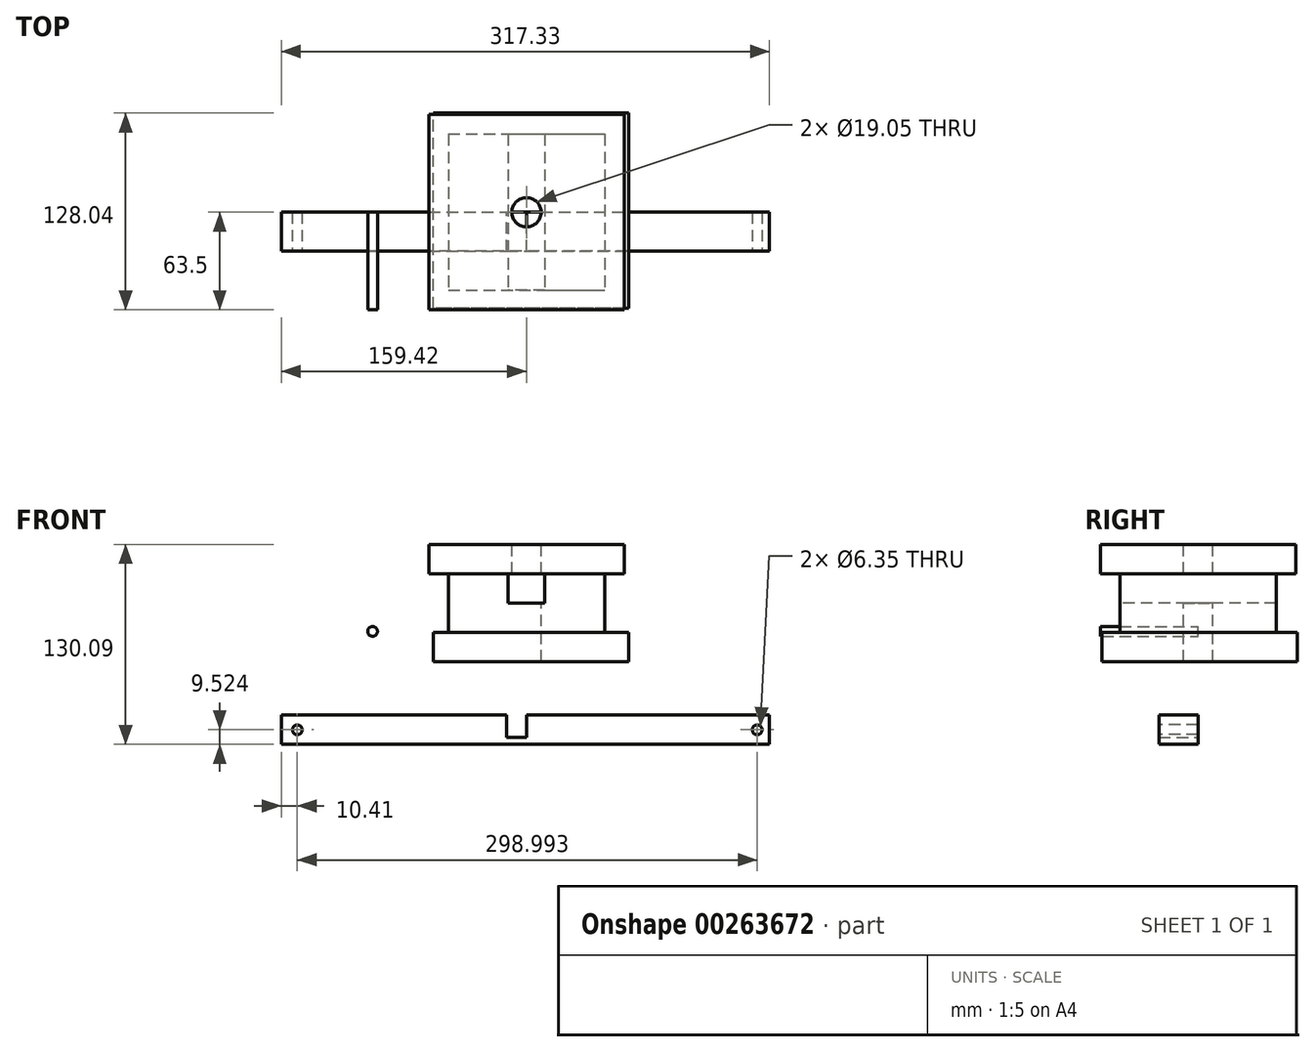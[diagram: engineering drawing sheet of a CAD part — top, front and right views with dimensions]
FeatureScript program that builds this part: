
annotation { "Feature Type Name" : "Feature", "Feature Type Description" : "" }
export const myFeature = defineFeature(function(context is Context, id is Id, definition is map)
    precondition{}
    {
        {
            var Q0;
            Q0=qCreatedBy(makeId("Top.planeOp"),FACE);
            var sketch = newSketch(context, id + "F0", { "sketchPlane" : qUnion([Q0])});
            skLineSegment(sketch, "E0", {"start": v(-60.56, 64.54) * mm, "end": v(66.44, 64.54) * mm});
            skLineSegment(sketch, "E1", {"start": v(66.44, 64.54) * mm, "end": v(66.44, -62.46) * mm});
            skLineSegment(sketch, "E2", {"start": v(66.44, -62.46) * mm, "end": v(-60.56, -62.46) * mm});
            skLineSegment(sketch, "E3", {"start": v(-60.56, -62.46) * mm, "end": v(-60.56, 64.54) * mm});
            skSolve(sketch);
        }
        {
            var Q0;
            Q0=makeQuery(id+"F0.imprint","IMPRINT",FACE,{"disambiguationData":[TD([[makeQuery(id+"F0.imprint","IMPRINT",EDGE,{"derivedFrom":sQuery(id+"F0.wireOp",EDGE,"E0")}),-1.0]])]});
            extrude(context, id + "F1", {"entities" : qUnion([Q0]), "depth" : 19.05 * mm});
        }
        {
            var Q0;
            Q0=makeQuery(id+"F1.opExtrude","CAP_FACE",FACE,{"disambiguationData":[OSD([sQuery(id+"F0.wireOp",EDGE,"E0"),sQuery(id+"F0.wireOp",EDGE,"E1"),sQuery(id+"F0.wireOp",EDGE,"E2"),sQuery(id+"F0.wireOp",EDGE,"E3")])],"isStart":false});
            var sketch = newSketch(context, id + "F2", { "sketchPlane" : qUnion([Q0])});
            skLineSegment(sketch, "E4.bottom", {"start": v(-50.8, 50.8) * mm, "end": v(50.8, 50.8) * mm});
            skLineSegment(sketch, "E4.top", {"start": v(-50.8, -50.8) * mm, "end": v(50.8, -50.8) * mm});
            skLineSegment(sketch, "E4.left", {"start": v(-50.8, 50.8) * mm, "end": v(-50.8, -50.8) * mm});
            skLineSegment(sketch, "E4.right", {"start": v(50.8, 50.8) * mm, "end": v(50.8, -50.8) * mm});
            skPoint(sketch, "E4.middle", {"position": v(0, 0) * mm});
            skSolve(sketch);
        }
        {
            var Q0;
            Q0=makeQuery(id+"F2.imprint","IMPRINT",FACE,{"disambiguationData":[TD([[makeQuery(id+"F2.imprint","IMPRINT",EDGE,{"derivedFrom":sQuery(id+"F2.wireOp",EDGE,"E4.bottom")}),-1.0]])]});
            extrude(context, id + "F3", {"entities" : qUnion([Q0]), "operationType" : NewBodyOperationType.ADD, "depth" : 38.1 * mm});
        }
        {
            var Q0;
            Q0=makeQuery(id+"F3.opExtrude","CAP_FACE",FACE,{"disambiguationData":[OSD([sQuery(id+"F2.wireOp",EDGE,"E4.bottom"),sQuery(id+"F2.wireOp",EDGE,"E4.top"),sQuery(id+"F2.wireOp",EDGE,"E4.left"),sQuery(id+"F2.wireOp",EDGE,"E4.right")])],"isStart":false});
            var sketch = newSketch(context, id + "F4", { "sketchPlane" : qUnion([Q0])});
            skLineSegment(sketch, "E5.bottom", {"start": v(-63.5, 63.5) * mm, "end": v(63.5, 63.5) * mm});
            skLineSegment(sketch, "E5.top", {"start": v(-63.5, -63.5) * mm, "end": v(63.5, -63.5) * mm});
            skLineSegment(sketch, "E5.left", {"start": v(-63.5, 63.5) * mm, "end": v(-63.5, -63.5) * mm});
            skLineSegment(sketch, "E5.right", {"start": v(63.5, 63.5) * mm, "end": v(63.5, -63.5) * mm});
            skPoint(sketch, "E5.middle", {"position": v(0, 0) * mm});
            skSolve(sketch);
        }
        {
            var Q0;
            Q0=makeQuery(id+"F4.imprint","IMPRINT",FACE,{"disambiguationData":[TD([[makeQuery(id+"F4.imprint","IMPRINT",EDGE,{"derivedFrom":sQuery(id+"F4.wireOp",EDGE,"E5.bottom")}),-1.0]])]});
            var Q1;
            Q1=makeQuery(id+"F4.imprint","IMPRINT",FACE,{"disambiguationData":[TD([[makeQuery(id+"F4.imprint","IMPRINT",EDGE,{"derivedFrom":makeQuery(id+"F3.opExtrude","CAP_EDGE",EDGE,{"disambiguationData":[OSD([sQuery(id+"F2.wireOp",EDGE,"E4.bottom")])],"isStart":false})}),-1.0]])]});
            extrude(context, id + "F5", {"entities" : qUnion([Q0, Q1]), "operationType" : NewBodyOperationType.ADD, "depth" : 19.05 * mm});
        }
        {
            var Q0;
            Q0=makeQuery(id+"F3.opExtrude","SWEPT_FACE",FACE,{"disambiguationData":[OSD([sQuery(id+"F2.wireOp",EDGE,"E4.top")])]});
            var sketch = newSketch(context, id + "F6", { "sketchPlane" : qUnion([Q0])});
            skPoint(sketch, "E6.start.orphan", {"position": v(-14.24, 44.1) * mm});
            skPoint(sketch, "E7.end.orphan", {"position": v(4.33, 44.1) * mm});
            skLineSegment(sketch, "E8", {"start": v(0, 19.05) * mm, "end": v(0, 38.1) * mm});
            skLineSegment(sketch, "E9.bottom", {"start": v(11.9, 57.15) * mm, "end": v(-11.9, 57.15) * mm});
            skLineSegment(sketch, "E9.top", {"start": v(11.9, 38.1) * mm, "end": v(-11.9, 38.1) * mm});
            skLineSegment(sketch, "E9.left", {"start": v(11.9, 57.15) * mm, "end": v(11.9, 38.1) * mm});
            skLineSegment(sketch, "E9.right", {"start": v(-11.9, 57.15) * mm, "end": v(-11.9, 38.1) * mm});
            skPoint(sketch, "E9.middle", {"position": v(0, 47.63) * mm});
            skPoint(sketch, "E10.start.orphan", {"position": v(0, 57.15) * mm});
            skSolve(sketch);
        }
        {
            var Q0;
            Q0=makeQuery(id+"F5.opExtrude","CAP_FACE",FACE,{"disambiguationData":[OSD([sQuery(id+"F4.wireOp",EDGE,"E5.bottom"),sQuery(id+"F4.wireOp",EDGE,"E5.top"),sQuery(id+"F4.wireOp",EDGE,"E5.left"),sQuery(id+"F4.wireOp",EDGE,"E5.right")])],"isStart":false});
            var sketch = newSketch(context, id + "F7", { "sketchPlane" : qUnion([Q0])});
            skPoint(sketch, "E11.start.orphan", {"position": v(-7.43, 0) * mm});
            skLineSegment(sketch, "E12", {"start": v(-7.43, 0) * mm, "end": v(0, 0) * mm});
            skSolve(sketch);
        }
        {
            var Q0;
            Q0=sQuery(id+"F7.wireOp",VERTEX,"E12.end");
            var Q1;
            Q1=makeQuery(id+"F1.opExtrude","SWEPT_BODY",BODY,{"disambiguationData":[OSD([sQuery(id+"F0.wireOp",EDGE,"E0"),sQuery(id+"F0.wireOp",EDGE,"E1"),sQuery(id+"F0.wireOp",EDGE,"E2"),sQuery(id+"F0.wireOp",EDGE,"E3")])]});
            hole(context, id + "F8", {"style" : HoleStyle.SIMPLE, "endStyle" : HoleEndStyle.THROUGH, "holeDiameter" : 19.05 * mm, "tappedDepth" : 12.7 * mm, "tapClearance" : 3, "locations" : qUnion([Q0]), "scope" : qUnion([Q1])});
        }
        {
            var Q0;
            Q0=makeQuery(id+"F6.imprint","IMPRINT",FACE,{"disambiguationData":[TD([[makeQuery(id+"F6.imprint","IMPRINT",EDGE,{"derivedFrom":sQuery(id+"F6.wireOp",EDGE,"E9.bottom")}),-1.0]])]});
            extrude(context, id + "F9", {"entities" : qUnion([Q0]), "operationType" : NewBodyOperationType.REMOVE, "endBound" : BoundingType.THROUGH_ALL, "oppositeDirection" : true, "depth" : 25.4 * mm});
        }
        {
            var Q0;
            Q0=qCreatedBy(makeId("Front.planeOp"),FACE);
            var sketch = newSketch(context, id + "F10", { "sketchPlane" : qUnion([Q0])});
            skLineSegment(sketch, "E13", {"start": v(157.91, -34.84) * mm, "end": v(157.91, -53.9) * mm});
            skLineSegment(sketch, "E14", {"start": v(157.91, -53.9) * mm, "end": v(-159.42, -53.9) * mm});
            skPoint(sketch, "E15.end.orphan", {"position": v(-164.43, -34.84) * mm});
            skLineSegment(sketch, "E16", {"start": v(-159.42, -34.84) * mm, "end": v(-159.42, -53.9) * mm});
            skLineSegment(sketch, "E17", {"start": v(-159.42, -34.84) * mm, "end": v(-13.03, -34.84) * mm});
            skPoint(sketch, "E18.end.orphan", {"position": v(18.55, -45.37) * mm});
            skPoint(sketch, "E19.end.orphan", {"position": v(0, -34.84) * mm});
            skLineSegment(sketch, "E20", {"start": v(18.55, -34.84) * mm, "end": v(157.91, -34.84) * mm});
            skLineSegment(sketch, "E21", {"start": v(0, -34.84) * mm, "end": v(18.55, -34.84) * mm});
            skPoint(sketch, "E22.end.orphan", {"position": v(14.04, -45.37) * mm});
            skPoint(sketch, "E23.end.orphan", {"position": v(0, -45.37) * mm});
            skPoint(sketch, "E24.end.orphan", {"position": v(-13.03, -45.37) * mm});
            skLineSegment(sketch, "E25", {"start": v(-13.03, -34.84) * mm, "end": v(-13.03, -49.38) * mm});
            skLineSegment(sketch, "E26", {"start": v(-13.03, -49.38) * mm, "end": v(0, -49.38) * mm});
            skLineSegment(sketch, "E27", {"start": v(0, -49.38) * mm, "end": v(0, -34.84) * mm});
            skLineSegment(sketch, "E28", {"start": v(-13.03, -44.37) * mm, "end": v(0, -44.37) * mm});
            skPoint(sketch, "E28.startSnap0", {"position": v(-159.42, -44.37) * mm});
            skPoint(sketch, "E29.orphan", {"position": v(-150.26, -44.37) * mm});
            skSolve(sketch);
        }
        {
            var Q0;
            Q0=makeQuery(id+"F10.imprint","IMPRINT",FACE,{"disambiguationData":[TD([[makeQuery(id+"F10.imprint","IMPRINT",EDGE,{"derivedFrom":sQuery(id+"F10.wireOp",EDGE,"E13")}),-1.0]])]});
            extrude(context, id + "F11", {"entities" : qUnion([Q0]), "depth" : 25.4 * mm});
        }
        {
            var Q0;
            Q0=makeQuery(id+"F11.opExtrude","CAP_FACE",FACE,{"disambiguationData":[OSD([sQuery(id+"F10.wireOp",EDGE,"E13"),sQuery(id+"F10.wireOp",EDGE,"E14"),sQuery(id+"F10.wireOp",EDGE,"E16"),sQuery(id+"F10.wireOp",EDGE,"E17"),sQuery(id+"F10.wireOp",EDGE,"E20"),sQuery(id+"F10.wireOp",EDGE,"E21"),sQuery(id+"F10.wireOp",EDGE,"E25"),sQuery(id+"F10.wireOp",EDGE,"E26"),sQuery(id+"F10.wireOp",EDGE,"E27")])],"isStart":false});
            var sketch = newSketch(context, id + "F12", { "sketchPlane" : qUnion([Q0])});
            skLineSegment(sketch, "E30", {"start": v(-149.01, -44.37) * mm, "end": v(149.98, -44.37) * mm});
            skPoint(sketch, "E30.startSnap0", {"position": v(-159.42, -44.37) * mm});
            skPoint(sketch, "E30.endSnap0", {"position": v(157.91, -44.37) * mm});
            skSolve(sketch);
        }
        {
            var Q0;
            Q0=sQuery(id+"F12.wireOp",VERTEX,"E30.start");
            var Q1;
            Q1=sQuery(id+"F12.wireOp",VERTEX,"E30.end");
            var Q2;
            Q2=makeQuery(id+"F11.opExtrude","SWEPT_BODY",BODY,{"disambiguationData":[OSD([sQuery(id+"F10.wireOp",EDGE,"E13"),sQuery(id+"F10.wireOp",EDGE,"E14"),sQuery(id+"F10.wireOp",EDGE,"E16"),sQuery(id+"F10.wireOp",EDGE,"E17"),sQuery(id+"F10.wireOp",EDGE,"E20"),sQuery(id+"F10.wireOp",EDGE,"E21"),sQuery(id+"F10.wireOp",EDGE,"E25"),sQuery(id+"F10.wireOp",EDGE,"E26"),sQuery(id+"F10.wireOp",EDGE,"E27")])]});
            hole(context, id + "F13", {"style" : HoleStyle.SIMPLE, "endStyle" : HoleEndStyle.THROUGH, "holeDiameter" : 6.35 * mm, "tappedDepth" : 12.7 * mm, "tapClearance" : 3, "locations" : qUnion([Q0, Q1]), "scope" : qUnion([Q2])});
        }
        {
            var Q0;
            Q0=qCreatedBy(makeId("Front.planeOp"),FACE);
            var sketch = newSketch(context, id + "F14", { "sketchPlane" : qUnion([Q0])});
            skCircle(sketch, "E31", {"center": v(-100.06, 19.63) * mm, "radius": 3.18 * mm});
            skSolve(sketch);
        }
        {
            var Q0;
            Q0=makeQuery(id+"F14.imprint","IMPRINT",FACE,{"disambiguationData":[TD([[makeQuery(id+"F14.imprint","IMPRINT",EDGE,{"derivedFrom":sQuery(id+"F14.wireOp",EDGE,"E31")}),1.0]])]});
            extrude(context, id + "F15", {"entities" : qUnion([Q0]), "depth" : 63.5 * mm});
        }
    });
